# Revit family: FS_Скамейка_Лукоморье_R16
name_source: partatom
category: Антураж
revit_build: Autodesk Revit 2016 (Build: 20160314_0715(x64)
units: mm (PartAtom-declared; Revit-internal decimal feet)

## family parameters
Всегда вертикально = Да
Источник визуального образа = Геометрия семейства
На основе рабочей плоскости = Нет
Общий = Нет
При загрузке вырезать с полостями = Нет
Точка расчета площади = Нет

## types (6) — shared parameters
ADSK_Код изделия = 6791
ADSK_Материал доски = FS_Древесина
ADSK_Материал крепления = FS_Цинк
ADSK_Материал опоры = FS_Краска_Черная
ADSK_Размер_Высота = 925 мм
ADSK_Размер_Ширина = 790 мм
URL = https://hobbyka.ru
Изготовитель = ООО 'Хоббика'
Комментарии к типоразмеру = Материалы: сталь, брус
zero-valued in all types: Высота

## per-type parameters (varying)
| type | ADSK_Размер_Длина | Стоимость |
| Скамейка парковая «Лукоморье» 0.6м | 600 мм | 8820 $ |
| Скамейка парковая «Лукоморье» 1.2м | 1200 мм | 9702 $ |
| Скамейка парковая «Лукоморье» 1.5м | 1500 мм | 10474 $ |
| Скамейка парковая «Лукоморье» 1.8м | 1800 мм | 11191 $ |
| Скамейка парковая «Лукоморье» 2.0м | 2000 мм | 15656 $ |
| Скамейка парковая «Лукоморье» 3.0м | 3000 мм | 16656 $ |

note: column(s) folded — value = type name in every type: ADSK_Наименование
